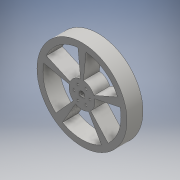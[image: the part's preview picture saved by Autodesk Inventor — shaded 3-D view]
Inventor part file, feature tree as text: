
AUTODESK INVENTOR PART (.ipt)
format: ipt  version: 2016 (Build 200138000, 138)  size: 156,160 bytes
history: native  units: mm
features: extrude x4, sketch x4, pattern_circular x2, other x1
ambient origin geometry x8: Origin, YZ Plane, XZ Plane, XY Plane, X Axis, Y Axis, Z Axis, Center Point
bodies: Body1 (feature_tree)
feature tree (11):
  other  "Sólido1"
  extrude  "Extrusión1"  Depth=8.0mm TaperAngle=0.0deg
  extrude  "Extrusión3"  Depth=3.0mm
  extrude  "Extrusión4"  Depth=8.0mm TaperAngle=0.0deg
  pattern_circular  "Patrón circular2"  [2 undecoded]
  extrude  "Extrusión5"  Depth=8.0mm TaperAngle=0.0deg
  pattern_circular  "Patrón circular3"  Count=6 Angle=360.0deg
  sketch  "Boceto2"  dims[d8=45.0mm d9=8.0mm d10=0.0mm]
  sketch  "Boceto4"  dims[d14=12.217305mm d24=3.0mm]
  sketch  "Boceto5"  dims[d25=1.0mm d26=8.0mm d27=0.0mm]
  sketch  "Boceto7"  dims[d28=1.0mm d29=4.0mm d30=8.0mm d31=0.0mm d32=60.0mm d33=360.0deg d37=13.0mm d38=39.0mm d39=120.0deg d40=60.0deg d41=8.0mm d42=0.0mm d43=50.0mm d44=360.0deg]
note: 2 required parameter values undecoded (feature->parameter linkage not recoverable at this tier; creation-order binding heuristic only, values carry confidence <= 0.55)
